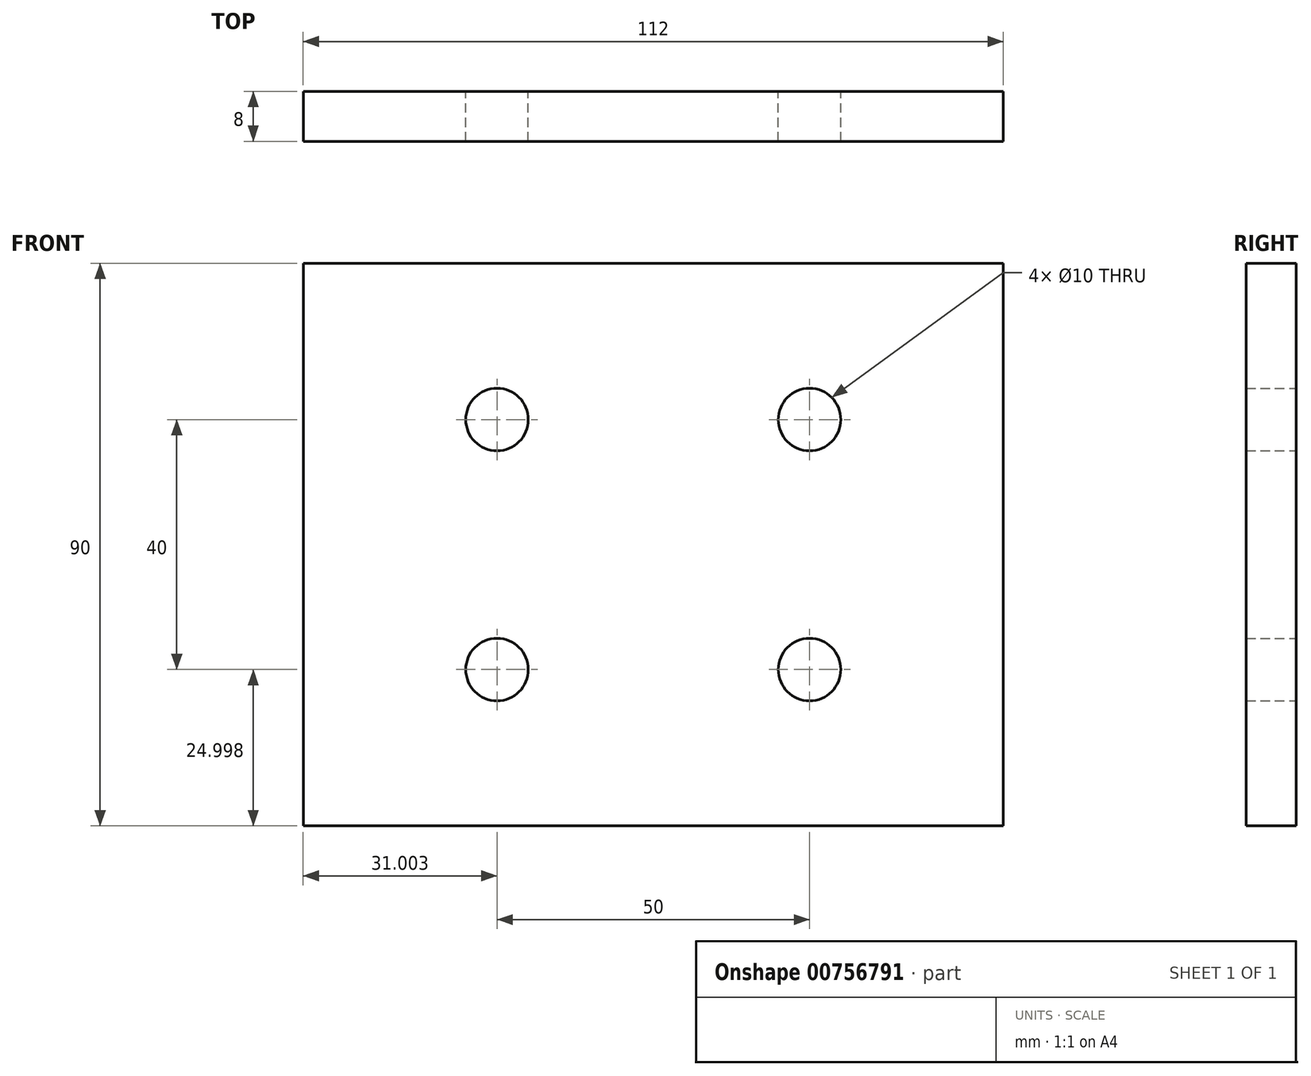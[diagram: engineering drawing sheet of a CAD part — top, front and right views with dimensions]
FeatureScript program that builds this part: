
annotation { "Feature Type Name" : "Feature", "Feature Type Description" : "" }
export const myFeature = defineFeature(function(context is Context, id is Id, definition is map)
    precondition{}
    {
        {
            var Q0;
            Q0=qCreatedBy(makeId("Front.planeOp"),FACE);
            var sketch = newSketch(context, id + "F0", { "sketchPlane" : qUnion([Q0])});
            skLineSegment(sketch, "E0.bottom", {"start": v(-56.45, 35.54) * mm, "end": v(55.55, 35.54) * mm});
            skLineSegment(sketch, "E0.top", {"start": v(-56.45, -54.46) * mm, "end": v(55.55, -54.46) * mm});
            skLineSegment(sketch, "E0.left", {"start": v(-56.45, 35.54) * mm, "end": v(-56.45, -54.46) * mm});
            skLineSegment(sketch, "E0.right", {"start": v(55.55, 35.54) * mm, "end": v(55.55, -54.46) * mm});
            skCircle(sketch, "E1", {"center": v(-25.45, 10.54) * mm, "radius": 5 * mm});
            skCircle(sketch, "E2", {"center": v(24.55, 10.54) * mm, "radius": 5 * mm});
            skCircle(sketch, "E3", {"center": v(-25.45, -29.46) * mm, "radius": 5 * mm});
            skCircle(sketch, "E4", {"center": v(24.55, -29.46) * mm, "radius": 5 * mm});
            skSolve(sketch);
        }
        {
            var Q0;
            Q0 = qSketchRegion(id + "F0", true);
            extrude(context, id + "F1", {"entities" : qUnion([Q0]), "depth" : 8 * mm, "offsetDistance" : 25 * mm});
        }
    });
